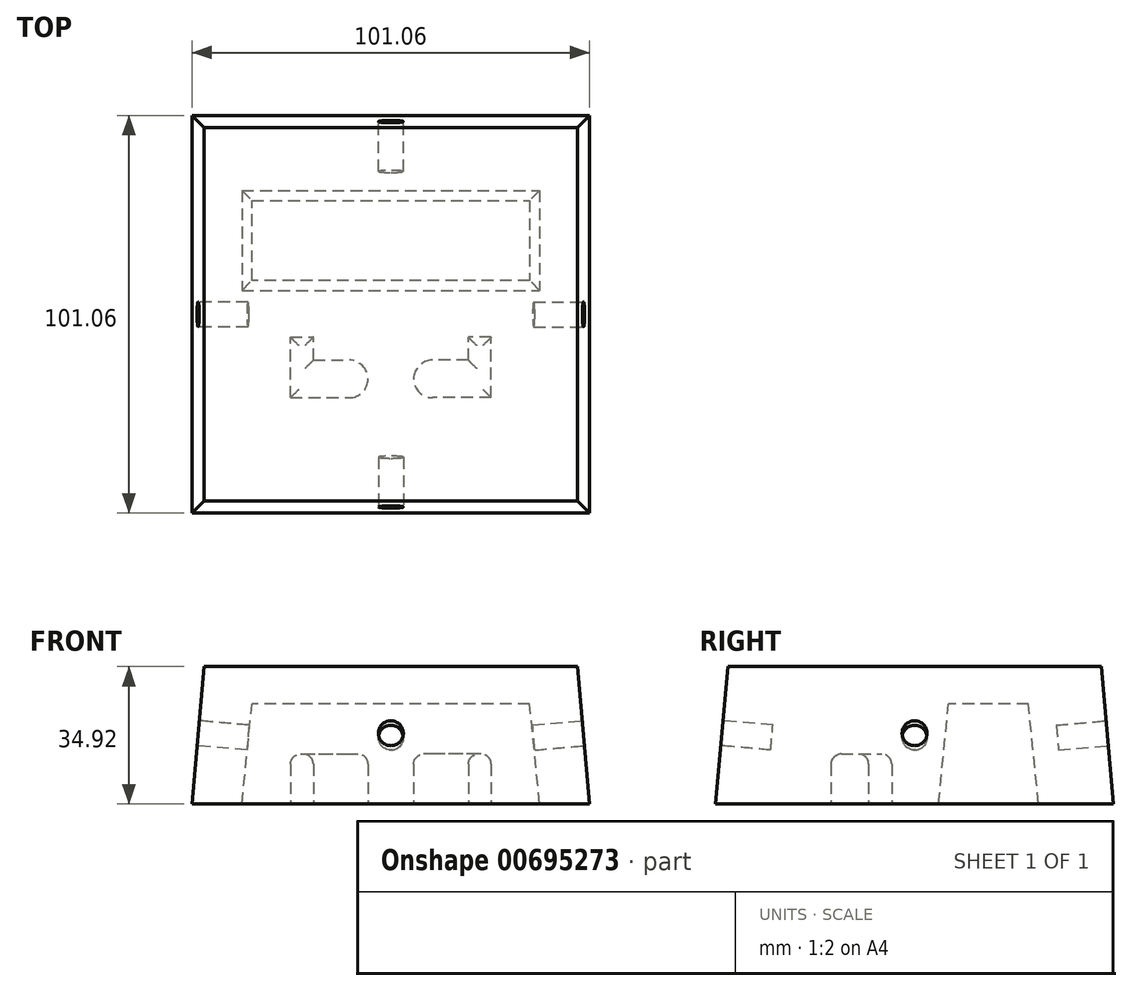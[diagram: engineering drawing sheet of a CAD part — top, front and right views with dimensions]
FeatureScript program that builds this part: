
annotation { "Feature Type Name" : "Feature", "Feature Type Description" : "" }
export const myFeature = defineFeature(function(context is Context, id is Id, definition is map)
    precondition{}
    {
        {
            var Q0;
            Q0=qCreatedBy(makeId("Top.planeOp"),FACE);
            var sketch = newSketch(context, id + "F0", { "sketchPlane" : qUnion([Q0])});
            skLineSegment(sketch, "E0.bottom", {"start": v(-50.8, -50.8) * mm, "end": v(50.8, -50.8) * mm});
            skLineSegment(sketch, "E0.top", {"start": v(-50.8, 50.8) * mm, "end": v(50.8, 50.8) * mm});
            skLineSegment(sketch, "E0.left", {"start": v(-50.8, -50.8) * mm, "end": v(-50.8, 50.8) * mm});
            skLineSegment(sketch, "E0.right", {"start": v(50.8, -50.8) * mm, "end": v(50.8, 50.8) * mm});
            skPoint(sketch, "E0.middle", {"position": v(0, 0) * mm});
            skSolve(sketch);
        }
        {
            var Q0;
            Q0=makeQuery(id+"F0.imprint","IMPRINT",FACE,{"disambiguationData":[TD([[makeQuery(id+"F0.imprint","IMPRINT",EDGE,{"derivedFrom":sQuery(id+"F0.wireOp",EDGE,"E0.bottom")}),1.0]])]});
            extrude(context, id + "F1", {"entities" : qUnion([Q0]), "depth" : 34.92 * mm, "offsetDistance" : 25.4 * mm});
        }
        {
            var Q0;
            Q0=makeQuery(id+"F1.opExtrude","CAP_FACE",FACE,{"disambiguationData":[OSD([sQuery(id+"F0.wireOp",EDGE,"E0.bottom"),sQuery(id+"F0.wireOp",EDGE,"E0.top"),sQuery(id+"F0.wireOp",EDGE,"E0.left"),sQuery(id+"F0.wireOp",EDGE,"E0.right")])],"isStart":false});
            chamfer(context, id + "F2", {"entities" : qUnion([Q0]), "chamferType" : ChamferType.OFFSET_ANGLE, "width" : 3.33 * mm, "oppositeDirection" : false, "angle" : 85 * degree, "tangentPropagation" : true});
        }
        {
            var Q0;
            Q0=makeQuery(id+"F2.opChamfer","BLEND_FACE",FACE,{"disambiguationData":[OSD([sQuery(id+"F0.wireOp",EDGE,"E0.top")])]});
            var sketch = newSketch(context, id + "F3", { "sketchPlane" : qUnion([Q0])});
            skLineSegment(sketch, "E1", {"start": v(50.53, -4.4) * mm, "end": v(-47.47, 30.65) * mm, "construction": true});
            skLineSegment(sketch, "E2", {"start": v(-50.53, -4.4) * mm, "end": v(47.47, 30.65) * mm, "construction": true});
            skCircle(sketch, "E3", {"center": v(0, 13.67) * mm, "radius": 3.18 * mm});
            skSolve(sketch);
        }
        {
            var Q0;
            Q0=makeQuery(id+"F3.imprint","IMPRINT",FACE,{"disambiguationData":[TD([[makeQuery(id+"F3.imprint","IMPRINT",EDGE,{"derivedFrom":sQuery(id+"F3.wireOp",EDGE,"E3")}),1.0]])]});
            extrude(context, id + "F4", {"entities" : qUnion([Q0]), "operationType" : NewBodyOperationType.REMOVE, "oppositeDirection" : true, "depth" : 12.7 * mm, "offsetDistance" : 25.4 * mm});
        }
        {
            var Q0;
            Q0=makeQuery(id+"F2.opChamfer","BLEND_FACE",FACE,{"disambiguationData":[OSD([sQuery(id+"F0.wireOp",EDGE,"E0.right")])]});
            var sketch = newSketch(context, id + "F5", { "sketchPlane" : qUnion([Q0])});
            skLineSegment(sketch, "E4", {"start": v(50.53, -4.4) * mm, "end": v(-47.47, 30.65) * mm, "construction": true});
            skLineSegment(sketch, "E5", {"start": v(-50.53, -4.4) * mm, "end": v(47.47, 30.65) * mm, "construction": true});
            skCircle(sketch, "E6", {"center": v(0, 13.67) * mm, "radius": 3.18 * mm});
            skSolve(sketch);
        }
        {
            var Q0;
            Q0=makeQuery(id+"F5.imprint","IMPRINT",FACE,{"disambiguationData":[TD([[makeQuery(id+"F5.imprint","IMPRINT",EDGE,{"derivedFrom":sQuery(id+"F5.wireOp",EDGE,"E6")}),1.0]])]});
            extrude(context, id + "F6", {"entities" : qUnion([Q0]), "operationType" : NewBodyOperationType.REMOVE, "oppositeDirection" : true, "depth" : 12.7 * mm, "offsetDistance" : 25.4 * mm});
        }
        {
            var Q0;
            Q0=makeQuery(id+"F2.opChamfer","BLEND_FACE",FACE,{"disambiguationData":[OSD([sQuery(id+"F0.wireOp",EDGE,"E0.bottom")])]});
            var sketch = newSketch(context, id + "F7", { "sketchPlane" : qUnion([Q0])});
            skLineSegment(sketch, "E7", {"start": v(50.53, -4.4) * mm, "end": v(-47.47, 30.65) * mm, "construction": true});
            skLineSegment(sketch, "E8", {"start": v(-50.53, -4.4) * mm, "end": v(47.47, 30.65) * mm, "construction": true});
            skCircle(sketch, "E9", {"center": v(0, 13.67) * mm, "radius": 3.18 * mm});
            skSolve(sketch);
        }
        {
            var Q0;
            Q0=makeQuery(id+"F7.imprint","IMPRINT",FACE,{"disambiguationData":[TD([[makeQuery(id+"F7.imprint","IMPRINT",EDGE,{"derivedFrom":sQuery(id+"F7.wireOp",EDGE,"E9")}),1.0]])]});
            extrude(context, id + "F8", {"entities" : qUnion([Q0]), "operationType" : NewBodyOperationType.REMOVE, "oppositeDirection" : true, "depth" : 12.7 * mm, "offsetDistance" : 25.4 * mm});
        }
        {
            var Q0;
            Q0=makeQuery(id+"F2.opChamfer","BLEND_FACE",FACE,{"disambiguationData":[OSD([sQuery(id+"F0.wireOp",EDGE,"E0.left")])]});
            var sketch = newSketch(context, id + "F9", { "sketchPlane" : qUnion([Q0])});
            skLineSegment(sketch, "E10", {"start": v(50.53, -4.4) * mm, "end": v(-47.47, 30.65) * mm, "construction": true});
            skLineSegment(sketch, "E11", {"start": v(47.47, 30.65) * mm, "end": v(-50.53, -4.4) * mm, "construction": true});
            skCircle(sketch, "E12", {"center": v(0, 13.67) * mm, "radius": 3.18 * mm});
            skSolve(sketch);
        }
        {
            var Q0;
            Q0=makeQuery(id+"F9.imprint","IMPRINT",FACE,{"disambiguationData":[TD([[makeQuery(id+"F9.imprint","IMPRINT",EDGE,{"derivedFrom":sQuery(id+"F9.wireOp",EDGE,"E12")}),1.0]])]});
            extrude(context, id + "F10", {"entities" : qUnion([Q0]), "operationType" : NewBodyOperationType.REMOVE, "oppositeDirection" : true, "depth" : 12.7 * mm, "offsetDistance" : 25.4 * mm});
        }
        {
            var Q0;
            Q0=makeQuery(id+"F1.opExtrude","CAP_FACE",FACE,{"disambiguationData":[OSD([sQuery(id+"F0.wireOp",EDGE,"E0.bottom"),sQuery(id+"F0.wireOp",EDGE,"E0.top"),sQuery(id+"F0.wireOp",EDGE,"E0.left"),sQuery(id+"F0.wireOp",EDGE,"E0.right")])],"isStart":true});
            var sketch = newSketch(context, id + "F11", { "sketchPlane" : qUnion([Q0])});
            skLineSegment(sketch, "E13.bottom", {"start": v(-50.53, -50.53) * mm, "end": v(-37.83, -50.53) * mm, "construction": true});
            skLineSegment(sketch, "E13.top", {"start": v(-50.53, -31.48) * mm, "end": v(-37.83, -31.48) * mm, "construction": true});
            skLineSegment(sketch, "E13.left", {"start": v(-50.53, -50.53) * mm, "end": v(-50.53, -31.48) * mm, "construction": true});
            skLineSegment(sketch, "E13.right", {"start": v(-37.83, -50.53) * mm, "end": v(-37.83, -31.48) * mm, "construction": true});
            skLineSegment(sketch, "E14.bottom", {"start": v(50.53, -50.53) * mm, "end": v(37.83, -50.53) * mm, "construction": true});
            skLineSegment(sketch, "E14.top", {"start": v(50.53, -31.48) * mm, "end": v(37.83, -31.48) * mm, "construction": true});
            skLineSegment(sketch, "E14.left", {"start": v(50.53, -50.53) * mm, "end": v(50.53, -31.48) * mm, "construction": true});
            skLineSegment(sketch, "E14.right", {"start": v(37.83, -50.53) * mm, "end": v(37.83, -31.48) * mm, "construction": true});
            skLineSegment(sketch, "E15.left", {"start": v(-37.83, -31.48) * mm, "end": v(-37.83, -31.48) * mm});
            skLineSegment(sketch, "E15.right", {"start": v(37.83, -31.48) * mm, "end": v(37.83, -31.48) * mm});
            skLineSegment(sketch, "E16.bottom", {"start": v(-37.83, -31.48) * mm, "end": v(37.83, -31.48) * mm});
            skLineSegment(sketch, "E16.top", {"start": v(-37.83, -6.08) * mm, "end": v(37.83, -6.08) * mm});
            skLineSegment(sketch, "E16.left", {"start": v(-37.83, -31.48) * mm, "end": v(-37.83, -6.08) * mm});
            skLineSegment(sketch, "E16.right", {"start": v(37.83, -31.48) * mm, "end": v(37.83, -6.08) * mm});
            skSolve(sketch);
        }
        {
            var Q0;
            Q0=makeQuery(id+"F11.imprint","IMPRINT",FACE,{"disambiguationData":[TD([[makeQuery(id+"F11.imprint","IMPRINT",EDGE,{"derivedFrom":sQuery(id+"F11.wireOp",EDGE,"E16.bottom")}),1.0]])]});
            extrude(context, id + "F12", {"entities" : qUnion([Q0]), "operationType" : NewBodyOperationType.REMOVE, "oppositeDirection" : true, "depth" : 25.4 * mm, "offsetDistance" : 25.4 * mm});
        }
        {
            var Q0;
            Q0=makeQuery(id+"F12.boolean.opBoolean","COPY",FACE,{"derivedFrom":makeQuery(id+"F12.opExtrude","CAP_FACE",FACE,{"disambiguationData":[OSD([sQuery(id+"F11.wireOp",EDGE,"E16.bottom"),sQuery(id+"F11.wireOp",EDGE,"E16.top"),sQuery(id+"F11.wireOp",EDGE,"E16.left"),sQuery(id+"F11.wireOp",EDGE,"E16.right")])],"isStart":false})});
            chamfer(context, id + "F13", {"entities" : qUnion([Q0]), "chamferType" : ChamferType.TWO_OFFSETS, "width1" : 2.54 * mm, "oppositeDirection" : false, "width2" : 25.4 * mm, "tangentPropagation" : true});
        }
        {
            var Q0;
            Q0=makeQuery(id+"F1.opExtrude","CAP_FACE",FACE,{"disambiguationData":[OSD([sQuery(id+"F0.wireOp",EDGE,"E0.bottom"),sQuery(id+"F0.wireOp",EDGE,"E0.top"),sQuery(id+"F0.wireOp",EDGE,"E0.left"),sQuery(id+"F0.wireOp",EDGE,"E0.right")])],"isStart":true});
            var sketch = newSketch(context, id + "F14", { "sketchPlane" : qUnion([Q0])});
            skLineSegment(sketch, "E17", {"start": v(0, 50.53) * mm, "end": v(0, -6.08) * mm, "construction": true});
            skArc(sketch, "E18", {"start": v(-10.55, 11.66) * mm, "mid": v(-5.8, 16.42) * mm, "end": v(-10.55, 21.19) * mm});
            skLineSegment(sketch, "E19.bottom", {"start": v(-25.49, 21.19) * mm, "end": v(-10.55, 21.19) * mm});
            skLineSegment(sketch, "E19.top", {"start": v(-19.7, 11.66) * mm, "end": v(-10.55, 11.66) * mm});
            skLineSegment(sketch, "E19.left", {"start": v(-25.49, 21.19) * mm, "end": v(-25.49, 11.66) * mm});
            skLineSegment(sketch, "E19.right", {"start": v(-10.55, 21.19) * mm, "end": v(-10.55, 21.19) * mm});
            skLineSegment(sketch, "E20.bottom", {"start": v(-25.49, 21.19) * mm, "end": v(-19.7, 21.19) * mm});
            skLineSegment(sketch, "E20.top", {"start": v(-25.49, 5.81) * mm, "end": v(-19.7, 5.81) * mm});
            skLineSegment(sketch, "E20.left", {"start": v(-25.49, 21.19) * mm, "end": v(-25.49, 5.81) * mm});
            skLineSegment(sketch, "E20.right", {"start": v(-19.7, 11.66) * mm, "end": v(-19.7, 5.81) * mm});
            skLineSegment(sketch, "E21.MirrorCS", {"start": v(10.55, 21.19) * mm, "end": v(10.55, 21.19) * mm});
            skLineSegment(sketch, "E22.MirrorCS", {"start": v(25.49, 21.19) * mm, "end": v(25.49, 11.66) * mm});
            skLineSegment(sketch, "E23.MirrorCS", {"start": v(19.7, 11.66) * mm, "end": v(19.7, 5.81) * mm});
            skLineSegment(sketch, "E24.MirrorCS", {"start": v(25.49, 21.19) * mm, "end": v(25.49, 5.81) * mm});
            skLineSegment(sketch, "E25.MirrorCS", {"start": v(25.49, 5.81) * mm, "end": v(19.7, 5.81) * mm});
            skLineSegment(sketch, "E26.MirrorCS", {"start": v(25.49, 21.19) * mm, "end": v(19.7, 21.19) * mm});
            skLineSegment(sketch, "E27.MirrorCS", {"start": v(25.49, 21.19) * mm, "end": v(10.55, 21.19) * mm});
            skLineSegment(sketch, "E28.MirrorCS", {"start": v(19.7, 11.66) * mm, "end": v(10.55, 11.66) * mm});
            skArc(sketch, "E29.MirrorCS", {"start": v(10.55, 11.66) * mm, "mid": v(5.8, 16.42) * mm, "end": v(10.55, 21.19) * mm});
            skSolve(sketch);
        }
        {
            var Q0;
            Q0 = qSketchRegion(id + "F14", true);
            extrude(context, id + "F15", {"entities" : qUnion([Q0]), "operationType" : NewBodyOperationType.REMOVE, "oppositeDirection" : true, "depth" : 12.7 * mm, "offsetDistance" : 25.4 * mm});
        }
        {
            var Q0;
            Q0=makeQuery(id+"F15.boolean.opBoolean","COPY",FACE,{"derivedFrom":makeQuery(id+"F15.opExtrude","CAP_FACE",FACE,{"disambiguationData":[OSD([sQuery(id+"F14.wireOp",EDGE,"E18"),sQuery(id+"F14.wireOp",EDGE,"E19.bottom"),sQuery(id+"F14.wireOp",EDGE,"E19.top"),sQuery(id+"F14.wireOp",EDGE,"E19.right"),sQuery(id+"F14.wireOp",EDGE,"E20.bottom"),sQuery(id+"F14.wireOp",EDGE,"E20.top"),sQuery(id+"F14.wireOp",EDGE,"E20.left"),sQuery(id+"F14.wireOp",EDGE,"E20.right")])],"isStart":false})});
            var Q1;
            Q1=makeQuery(id+"F15.boolean.opBoolean","COPY",FACE,{"derivedFrom":makeQuery(id+"F15.opExtrude","CAP_FACE",FACE,{"disambiguationData":[OSD([sQuery(id+"F14.wireOp",EDGE,"E21.MirrorCS"),sQuery(id+"F14.wireOp",EDGE,"E23.MirrorCS"),sQuery(id+"F14.wireOp",EDGE,"E24.MirrorCS"),sQuery(id+"F14.wireOp",EDGE,"E25.MirrorCS"),sQuery(id+"F14.wireOp",EDGE,"E27.MirrorCS"),sQuery(id+"F14.wireOp",EDGE,"E28.MirrorCS"),sQuery(id+"F14.wireOp",EDGE,"E29.MirrorCS")])],"isStart":false})});
            fillet(context, id + "F16", {"entities" : qUnion([Q0, Q1]), "radius" : 2.54 * mm, "tangentPropagation" : true, "allowEdgeOverflow" : false});
        }
    });
